# Revit family: Template Enclosure Europe NoHosted
name_source: partatom
category: Electrical Equipment
units: mm (PartAtom-declared; Revit-internal decimal feet)

## family parameters
Always vertical = Yes
Cut with Voids When Loaded = No
Maintain Annotation Orientation = No
Panel Configuration = Two Columns, Circuits Across
Part Type = Panelboard
Room Calculation Point = No
Round Connector Dimension = Use Diameter
Shared = No
Work Plane-Based = Yes

## types (1)
- Template-Enclosure_EU-EC000214
    BC_METADATA = {"ObjectGuid":"bc35c96e-cb38-443e-833d-0616858cb9ac","ModelGuid":"8af03f69-2293-4735-a617-cc53adf55621","VariantGuid":"8b6e323b-1b53-409a-a940-11b5a7fc5337","Revision":"#4","VariantName":"Template-Enclosure_EU-EC000214"}
    Built-in depth = 150 mm
    Built-in height = 450 mm  [stored 1.47638 ft]
    Built-in width = 450 mm  [stored 1.47638 ft]
    Code hager = ADD-EC000214_EU
    DIN-rail = No
    Default Elevation = 1200 mm
    Depth = 250 mm  [stored 0.82021 ft]
    EF000024 - UV resistant = No
    EMC-version = Yes
    ETIM class code = EC000214
    ETIM class name = Small distribution board
    Earthing terminal block = Yes
    Extension possible = Yes
    HG000001-Number of columns = 3
    HG000002-With door or cover = Yes
    HG000005-Thickness = 3 mm  [stored 0.00984252 ft]
    HG000006-Flush mounted = Yes
    HG000007-Number of empty columns = 1
    HG000008-Number of empty rows = 0
    HG000009-Double swing door = Yes
    HG000010-Asymmetric doors = Yes
    HG000011-Empty rows from bottom = Yes
    HG000012-Door swing angle = 45.00°
    HG000013-Door on the left = No
    HG000014-Door on the right = Yes
    HG000015-Clearance visibility = Yes
    HG000016-Door 3D visibility = Yes
    HG000017-Distance between poles = 18 mm  [stored 0.0590551 ft]
    HG000060-RAL-number = 9010
    HGEF000266-Number of rows = 3
    HGEF002950-Width in number of modular spacings = 15
    Height = 500 mm  [stored 1.64042 ft]
    Inner depth = 0 mm  [stored 0 ft]
    Manufacturer = Hager
    Name BIM&CO = Electricity
    Name hager = ADD_Enclosures_EC000214
    Neutral terminal block = Yes
    Number of rows = 2
    RAL-number = 9010
    Reference = Template-Enclosure_EU-EC000214
    Signal passing door = Yes
    Transparent cover/door = Yes
    Uniformat = Low Tension Service & Dist.
    Uniformat code = D501001
    Width = 500 mm  [stored 1.64042 ft]
    Width in number of modular spacings = 15
    With lock = Yes
    With mounting plate = Yes

note: [stored X ft] marks values corroborated as IEEE doubles in the binary element streams (Revit-internal decimal feet)

## geometry (parser evidence)
native form markers: Sweep x20
no freeform markers — native parametric forms only
